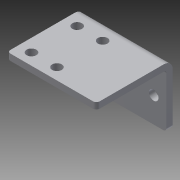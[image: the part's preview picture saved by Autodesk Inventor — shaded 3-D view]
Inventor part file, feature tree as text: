
AUTODESK INVENTOR PART (.ipt)
format: ipt  version: 2014 (Build 180170000, 170)  size: 137,728 bytes
history: native  units: in
note: dims shown in document units (in); Inventor stores cm internally (conversion verified against a paired STEP export)
features: sheet_metal_op x4, sketch x3, other x2, fillet x1, extrude x1
ambient origin geometry x8: Origin, YZ Plane, XZ Plane, XY Plane, X Axis, Y Axis, Z Axis, Center Point
bodies: Solid1 (feature_tree)
feature tree (11):
  sheet_metal_op  "Face1"
  sheet_metal_op  "Flange1"
  fillet  "Fillet1"  Radius=1.75in
  extrude  "Extrusion1"  Depth=0.19in
  sketch  "Sketch1"  dims[d1=1.0in d2=0.19in]
  other  "Plate1"
  sketch  "Sketch2"  dims[d4=0.7874in d6=1.0in d7=0.3937in d9=1.0in]
  other  "Plate2"
  sheet_metal_op  "Bend1"
  sheet_metal_op  "Corner1"
  sketch  "Sketch3"  dims[d11=0.125in d12=0.125in d13=0.0625in d14=0.25in d15=0.125in d16=1.5in d17=90.0deg d18=0.05in d19=0.5in d20=0.125in d21=0.125in d22=0.0625in d23=1.35in d24=0.75in d27=0.19in d28=0.125in d29=0.2265in d30=1.0in d31=0.0in d32=0.25in d33=0.875in]
